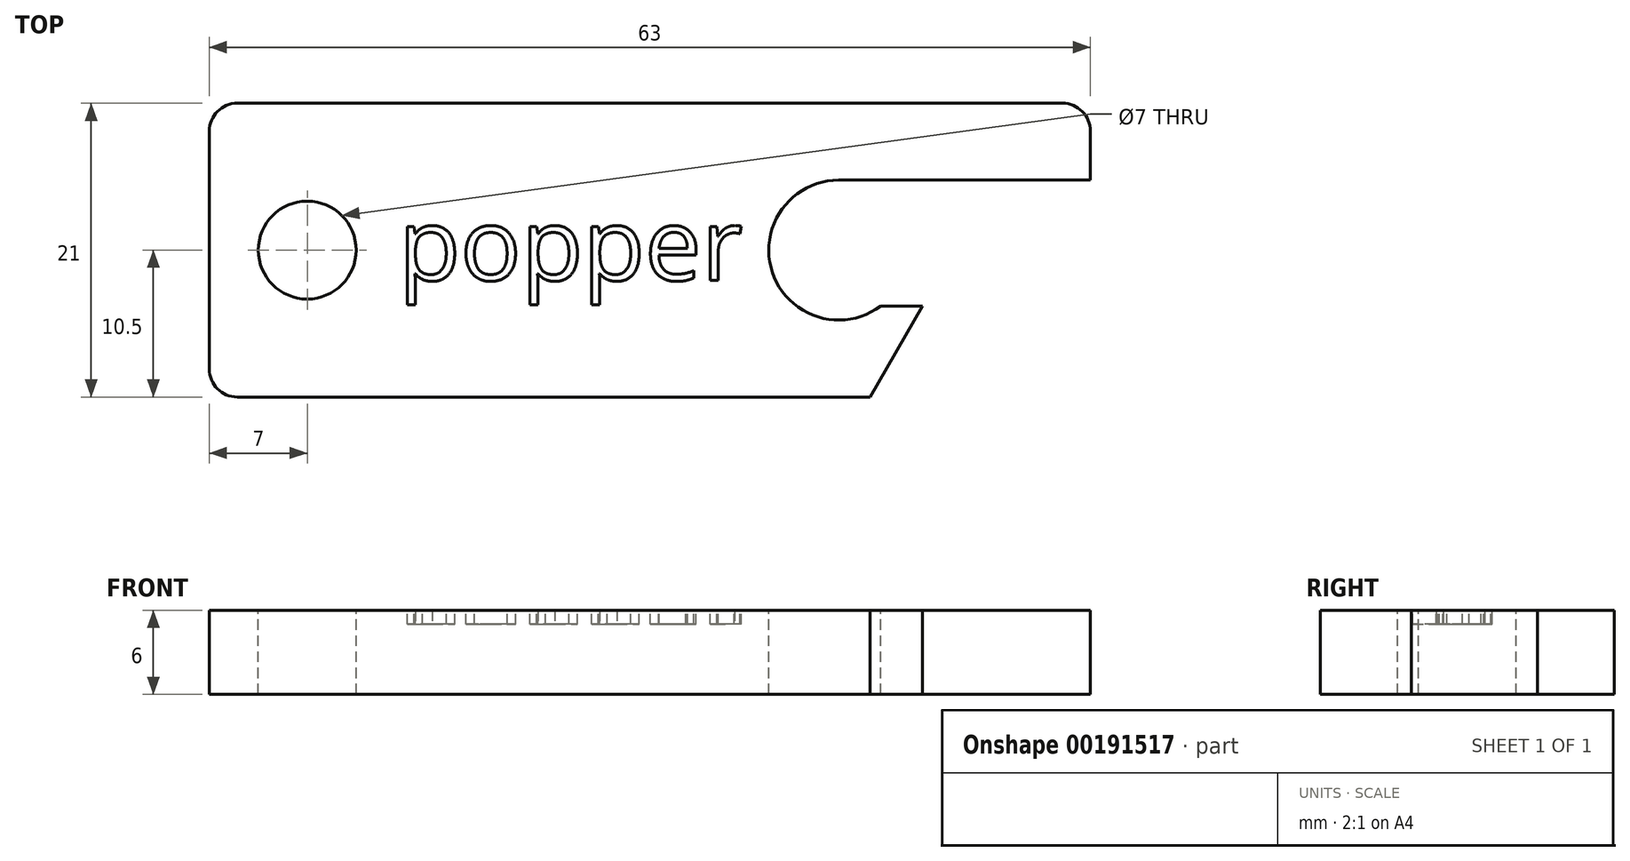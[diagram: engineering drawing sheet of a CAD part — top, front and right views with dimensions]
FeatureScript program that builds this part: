
annotation { "Feature Type Name" : "Feature", "Feature Type Description" : "" }
export const myFeature = defineFeature(function(context is Context, id is Id, definition is map)
    precondition{}
    {
        {
            var Q0;
            Q0=qCreatedBy(makeId("Top.planeOp"),FACE);
            var sketch = newSketch(context, id + "F0", { "sketchPlane" : qUnion([Q0])});
            skLineSegment(sketch, "E0.bottom", {"start": v(0, 0) * mm, "end": v(63, 0) * mm});
            skLineSegment(sketch, "E0.top", {"start": v(0, 21) * mm, "end": v(63, 21) * mm});
            skLineSegment(sketch, "E0.left", {"start": v(0, 0) * mm, "end": v(0, 21) * mm});
            skLineSegment(sketch, "E0.right", {"start": v(63, 0) * mm, "end": v(63, 21) * mm});
            skSolve(sketch);
        }
        {
            var Q0;
            Q0 = qSketchRegion(id + "F0", true);
            extrude(context, id + "F1", {"entities" : qUnion([Q0]), "flatOperationType" : FlatOperationType.REMOVE, "offsetDistance" : 25 * mm, "depth" : 6 * mm, "domain" : OperationDomain.MODEL});
        }
        {
            var Q0;
            Q0=makeQuery(id+"F1.opExtrude","CAP_FACE",FACE,{"disambiguationData":[OSD([sQuery(id+"F0.wireOp",EDGE,"E0.bottom"),sQuery(id+"F0.wireOp",EDGE,"E0.top"),sQuery(id+"F0.wireOp",EDGE,"E0.left"),sQuery(id+"F0.wireOp",EDGE,"E0.right")])],"isStart":false});
            var sketch = newSketch(context, id + "F2", { "sketchPlane" : qUnion([Q0])});
            skLineSegment(sketch, "E1", {"start": v(-14.14, 10.5) * mm, "end": v(74.82, 10.5) * mm, "construction": true});
            skArc(sketch, "E2", {"start": v(45, 15.5) * mm, "mid": v(40.26, 8.92) * mm, "end": v(48, 6.5) * mm});
            skLineSegment(sketch, "E3", {"start": v(63, 15.5) * mm, "end": v(45, 15.5) * mm});
            skLineSegment(sketch, "E4", {"start": v(51, 6.5) * mm, "end": v(48, 6.5) * mm});
            skLineSegment(sketch, "E5", {"start": v(51, 6.5) * mm, "end": v(47.25, 0) * mm});
            skLineSegment(sketch, "E6", {"start": v(47.25, 0) * mm, "end": v(63, 0) * mm});
            skLineSegment(sketch, "E7", {"start": v(63, 0) * mm, "end": v(63, 15.5) * mm});
            skSolve(sketch);
        }
        {
            var Q0;
            Q0 = qSketchRegion(id + "F2", true);
            extrude(context, id + "F3", {"entities" : qUnion([Q0]), "operationType" : NewBodyOperationType.REMOVE, "endBound" : BoundingType.THROUGH_ALL, "oppositeDirection" : true, "depth" : 25 * mm});
        }
        {
            var Q0;
            Q0=makeQuery(id+"F1.opExtrude","CAP_FACE",FACE,{"disambiguationData":[OSD([sQuery(id+"F0.wireOp",EDGE,"E0.bottom"),sQuery(id+"F0.wireOp",EDGE,"E0.top"),sQuery(id+"F0.wireOp",EDGE,"E0.left"),sQuery(id+"F0.wireOp",EDGE,"E0.right")])],"isStart":false});
            var sketch = newSketch(context, id + "F4", { "sketchPlane" : qUnion([Q0])});
            skLineSegment(sketch, "E8", {"start": v(-10.72, 10.5) * mm, "end": v(66.46, 10.5) * mm, "construction": true});
            skCircle(sketch, "E9", {"center": v(7, 10.5) * mm, "radius": 3.5 * mm});
            skSolve(sketch);
        }
        {
            var Q0;
            Q0 = qSketchRegion(id + "F4", true);
            extrude(context, id + "F5", {"entities" : qUnion([Q0]), "operationType" : NewBodyOperationType.REMOVE, "endBound" : BoundingType.THROUGH_ALL, "oppositeDirection" : true, "depth" : 25 * mm});
        }
        {
            var Q0;
            Q0=makeQuery(id+"F3.boolean.opBoolean","COPY",EDGE,{"derivedFrom":makeQuery(id+"F3.opExtrude","SWEPT_EDGE",EDGE,{"disambiguationData":[OSD([sQuery(id+"F0.wireOp",EDGE,"E0.bottom"),sQuery(id+"F2.wireOp",EDGE,"E5"),sQuery(id+"F2.wireOp",EDGE,"E6")])]})});
            var Q1;
            Q1=makeQuery(id+"F3.boolean.opBoolean","COPY",EDGE,{"derivedFrom":makeQuery(id+"F3.opExtrude","SWEPT_EDGE",EDGE,{"disambiguationData":[OSD([sQuery(id+"F0.wireOp",EDGE,"E0.right"),sQuery(id+"F2.wireOp",EDGE,"E3"),sQuery(id+"F2.wireOp",EDGE,"E7")])]})});
            var Q2;
            Q2=makeQuery(id+"F1.opExtrude","SWEPT_EDGE",EDGE,{"disambiguationData":[OSD([sQuery(id+"F0.wireOp",EDGE,"E0.top"),sQuery(id+"F0.wireOp",EDGE,"E0.right")])]});
            var Q3;
            Q3=makeQuery(id+"F1.opExtrude","SWEPT_EDGE",EDGE,{"disambiguationData":[OSD([sQuery(id+"F0.wireOp",EDGE,"E0.top"),sQuery(id+"F0.wireOp",EDGE,"E0.left")])]});
            var Q4;
            Q4=makeQuery(id+"F1.opExtrude","SWEPT_EDGE",EDGE,{"disambiguationData":[OSD([sQuery(id+"F0.wireOp",EDGE,"E0.bottom"),sQuery(id+"F0.wireOp",EDGE,"E0.left")])]});
            fillet(context, id + "F6", {"entities" : qUnion([Q0, Q1, Q2, Q3, Q4]), "radius" : 2 * mm, "tangentPropagation" : true, "allowEdgeOverflow" : false});
        }
        {
            var Q0;
            Q0=makeQuery(id+"F1.opExtrude","CAP_FACE",FACE,{"disambiguationData":[OSD([sQuery(id+"F0.wireOp",EDGE,"E0.bottom"),sQuery(id+"F0.wireOp",EDGE,"E0.top"),sQuery(id+"F0.wireOp",EDGE,"E0.left"),sQuery(id+"F0.wireOp",EDGE,"E0.right")])],"isStart":false});
            var sketch = newSketch(context, id + "F7", { "sketchPlane" : qUnion([Q0])});
            skText(sketch, "E10", { "text": "popper\n", "fontName": "OpenSans-Regular.ttf"});
            const initialGuessF7  = {"E10": [0.01353, 0.00833, 1, 0, 0.00519]};
            skSetInitialGuess(sketch, initialGuessF7);
            skSolve(sketch);
        }
        {
            var Q0;
            Q0 = qSketchRegion(id + "F7", true);
            extrude(context, id + "F8", {"entities" : qUnion([Q0]), "operationType" : NewBodyOperationType.REMOVE, "flatOperationType" : FlatOperationType.REMOVE, "oppositeDirection" : true, "depth" : 1 * mm, "offsetDistance" : 25 * mm, "domain" : OperationDomain.MODEL});
        }
    });
